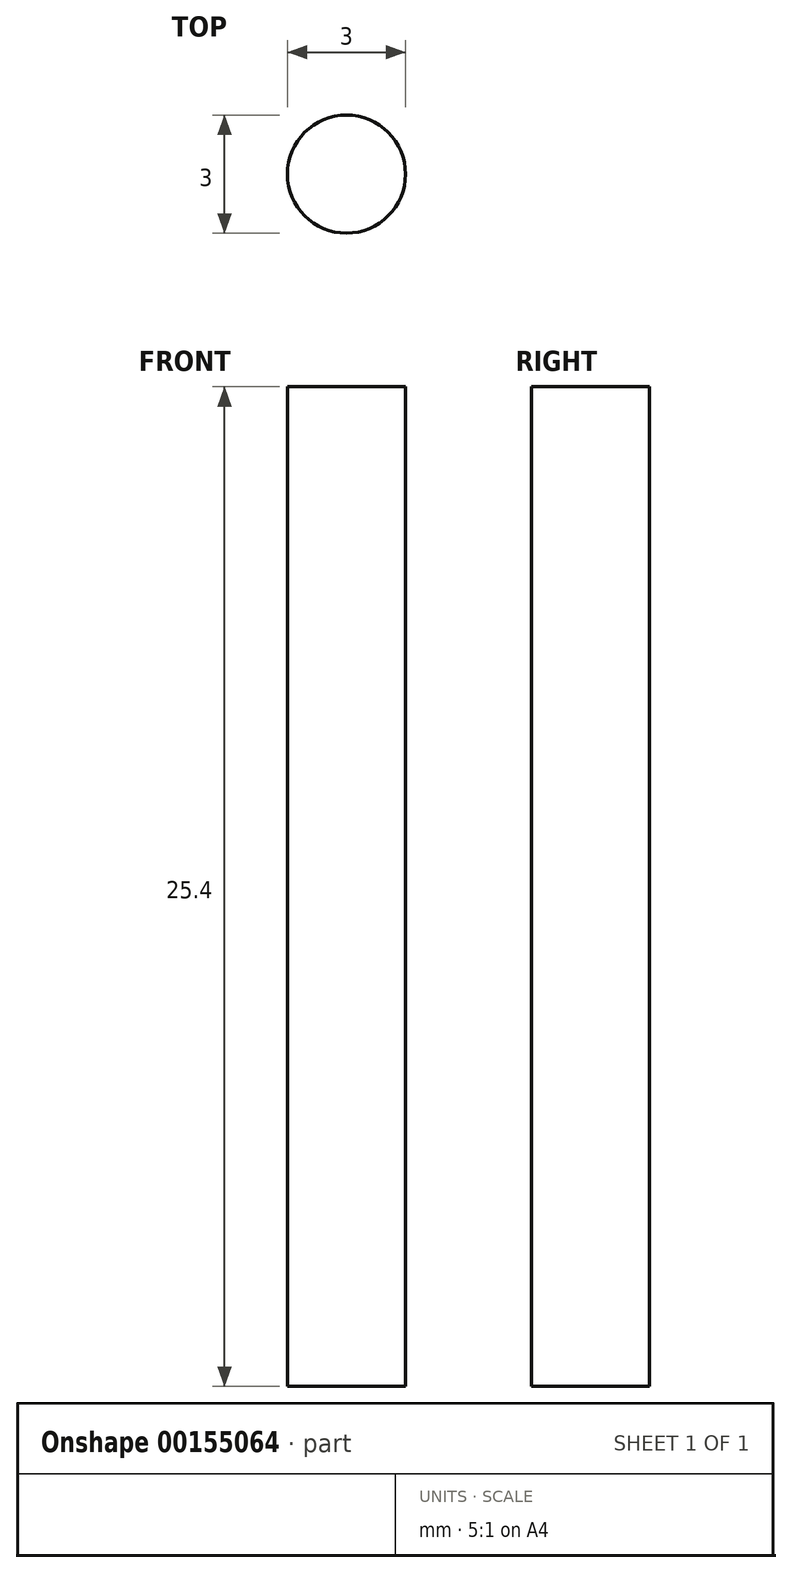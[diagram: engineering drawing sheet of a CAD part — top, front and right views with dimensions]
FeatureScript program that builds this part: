
annotation { "Feature Type Name" : "Feature", "Feature Type Description" : "" }
export const myFeature = defineFeature(function(context is Context, id is Id, definition is map)
    precondition{}
    {
        {
            var Q0;
            Q0=qCreatedBy(makeId("Top.planeOp"),FACE);
            var sketch = newSketch(context, id + "F0", { "sketchPlane" : qUnion([Q0])});
            skCircle(sketch, "E0", {"center": v(0, 0) * mm, "radius": 1.5 * mm});
            skSolve(sketch);
        }
        {
            var Q0;
            Q0=makeQuery(id+"F0.imprint","IMPRINT",FACE,{"disambiguationData":[TD([[makeQuery(id+"F0.imprint","IMPRINT",EDGE,{"derivedFrom":sQuery(id+"F0.wireOp",EDGE,"E0")}),1.0]])]});
            extrude(context, id + "F1", {"entities" : qUnion([Q0]), "depth" : 25.4 * mm});
        }
    });
